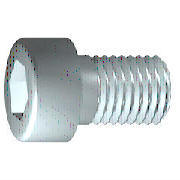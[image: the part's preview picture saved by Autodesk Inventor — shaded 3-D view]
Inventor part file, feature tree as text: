
AUTODESK INVENTOR PART (.ipt)
format: ipt  version: 2020 (Build 240168000, 168)  size: 192,512 bytes
history: native  units: mm (DEFAULTED — no unit token found)
features: sketch x2, extrude x1, plane x1, fillet x1
ambient origin geometry x7: Origin, YZ Plane, XY Plane, X Axis, Y Axis, Z Axis, Center Point
bodies: Solid1 (feature_tree), Body (feature_tree)
feature tree (5):
  extrude  "Slot"  Depth=3.0mm
  plane  "Work Plane1"
  fillet  "Fillet2"  Radius=3.0mm
  sketch  "Sketch1"  dims[d1=14.75mm d2=0.306825mm d3=3.0mm]
  sketch  "Sketch2"  dims[d4=1.3mm d5=60.0deg d6=3.0mm d7=3.0mm d8=2.886751mm d9=5.5mm d10=90.0deg d11=10.0mm d12=0.0mm d13=14.75mm d14=0.0mm d15=0.306725mm d16=0.306725mm d17=0.3mm d19=0.0mm d26=16.0mm d27=45.0deg d28=0.0mm d29=0.0mm d30=0.1mm]
